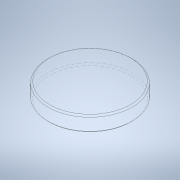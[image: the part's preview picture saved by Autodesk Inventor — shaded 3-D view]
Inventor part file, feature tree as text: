
AUTODESK INVENTOR PART (.ipt)
format: ipt  version: 2022 (Build 260153000, 153)  size: 112,128 bytes
history: native  units: mm
features: extrude x1, chamfer x1, sketch x1
ambient origin geometry x8: Origin, YZ Plane, XZ Plane, XY Plane, X Axis, Y Axis, Z Axis, Center Point
bodies: Volumenkörper1 (feature_tree)
feature tree (3):
  extrude  "Extrusion1"  Depth=10.0mm
  chamfer  "Fase1"  Distance=1.0mm Angle=45.0deg
  sketch  "Skizze1"  dims[d0=10.0mm d1=0.0mm d2=55.5mm d3=1.0mm d4=2.0mm d5=45.0deg]
